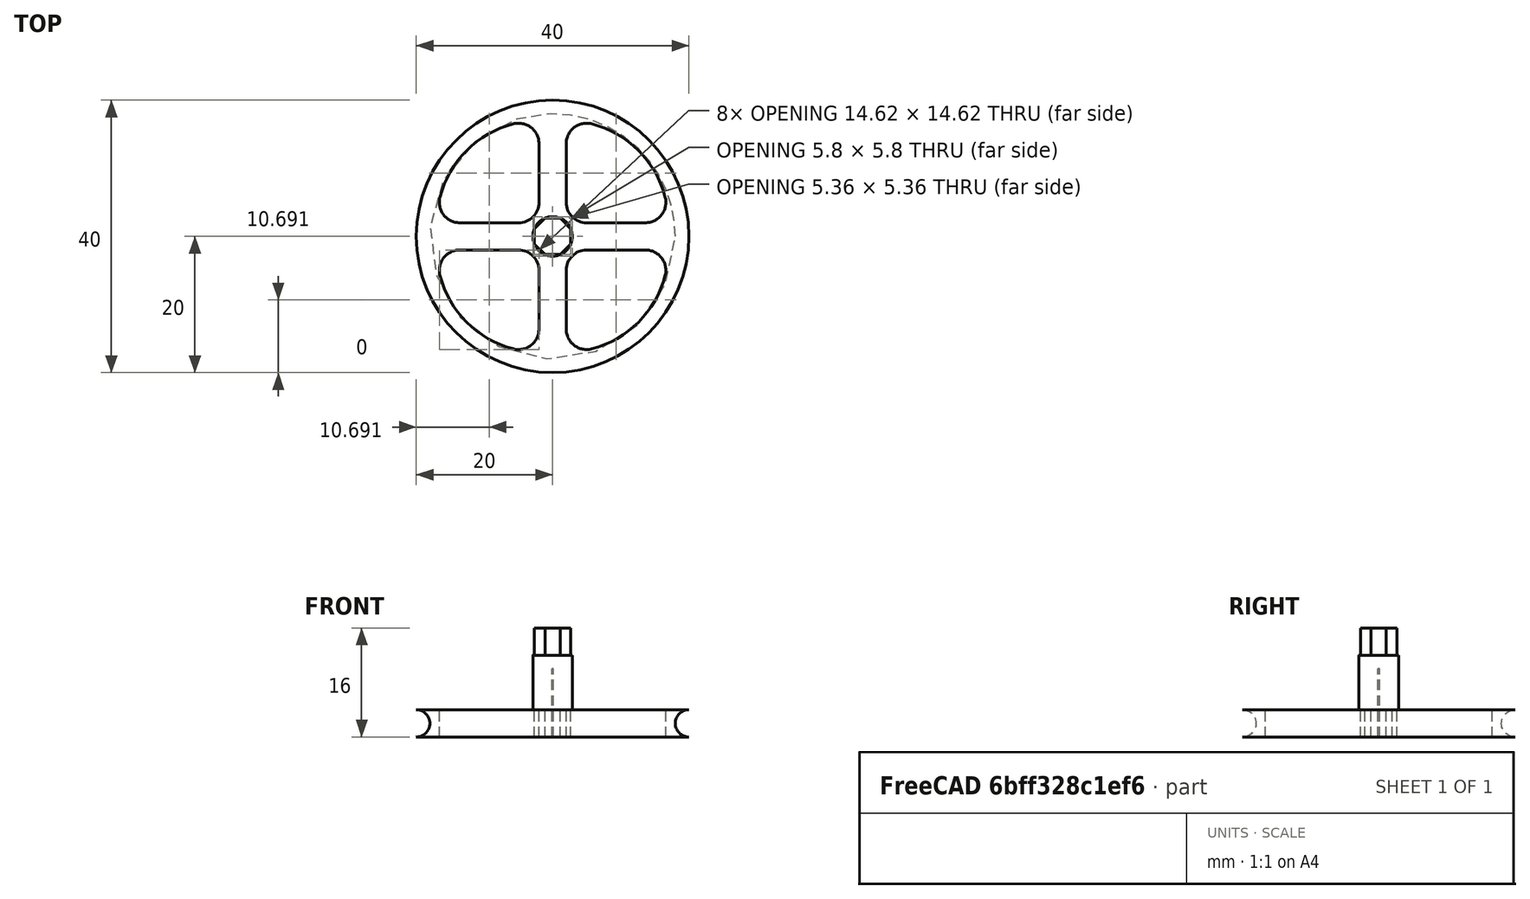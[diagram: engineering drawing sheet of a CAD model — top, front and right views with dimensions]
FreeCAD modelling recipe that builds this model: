
FCSTD DOCUMENT  (FreeCAD 0.18.1R)
Label: wheel right front techdraw
License: All rights reserved
LicenseURL: http://en.wikipedia.org/wiki/All_rights_reserved
objects: TechDraw::DrawViewDimension×7, PartDesign::Plane×4, TechDraw::DrawProjGroupItem×4, Part::Cylinder×3, Sketcher::SketchObject×3, PartDesign::Fillet×3, PartDesign::Body×3, PartDesign::FeatureBase×2, PartDesign::Pocket×2, Part::MultiFuse×2, App::Part×2, Part::Torus×1, Part::Cut×1, App::MeasureDistance×1, PartDesign::ShapeBinder×1, PartDesign::Pad×1, TechDraw::DrawSVGTemplate×1, TechDraw::DrawProjGroup×1, TechDraw::DrawPage×1
note: 29 computed .brp shape members not serialized (recipe doc carries the construction recipe); baked Part::Feature solids carry a one-line shape summary decoded from their .brp

FEATURE [Part::Cylinder] Cylinder
  Angle = 360
  AttacherType = Attacher::AttachEngine3D
  Height = 4
  Radius = 20
FEATURE [Part::Cylinder] Cylinder001
  Angle = 360
  AttacherType = Attacher::AttachEngine3D
  Height = 10
  Radius = 0.1
FEATURE [PartDesign::FeatureBase] BaseFeature
  BaseFeature = -> Cylinder
FEATURE [PartDesign::Plane] DatumPlane
  Length = 47.9863
  MapMode = 5
  Placement = pos=(0,0,0) rot=(1,0,0;3.14159rad)
  ResizeMode = 0
  Support = -> [BaseFeature]
  Width = 47.8497
FEATURE [Sketcher::SketchObject] Sketch001
  MapMode = 5
  Placement = pos=(0,0,0) rot=(1,0,0;3.14159rad)
  Support = -> [DatumPlane]
  sketch-geometry (12):
    g0: LineSegment StartX=2 StartY=17 StartZ=0 EndX=2 EndY=2 EndZ=0
    g1: LineSegment StartX=-2 StartY=17 StartZ=0 EndX=-2 EndY=2 EndZ=0
    g2: LineSegment StartX=2 StartY=2 StartZ=0 EndX=17 EndY=2 EndZ=0
    g3: LineSegment StartX=2 StartY=-2 StartZ=0 EndX=17 EndY=-2 EndZ=0
    g4: LineSegment StartX=-2 StartY=-2 StartZ=0 EndX=-2 EndY=-17 EndZ=0
    g5: LineSegment StartX=-17 StartY=-2 StartZ=0 EndX=-2 EndY=-2 EndZ=0
    g6: LineSegment StartX=-17 StartY=2 StartZ=0 EndX=-2 EndY=2 EndZ=0
    g7: LineSegment StartX=2 StartY=-2 StartZ=0 EndX=2 EndY=-17 EndZ=0
    g8: ArcOfCircle CenterX=2 CenterY=2 CenterZ=0 NormalX=0 NormalY=0 NormalZ=1 AngleXU=0 Radius=15 StartAngle=0 EndAngle=1.5708
    g9: ArcOfCircle CenterX=-2 CenterY=2 CenterZ=0 NormalX=0 NormalY=0 NormalZ=1 AngleXU=0 Radius=15 StartAngle=1.5708 EndAngle=3.14159
    g10: ArcOfCircle CenterX=-2 CenterY=-2 CenterZ=0 NormalX=0 NormalY=0 NormalZ=1 AngleXU=0 Radius=15 StartAngle=3.14159 EndAngle=4.71239
    g11: ArcOfCircle CenterX=2 CenterY=-2 CenterZ=0 NormalX=0 NormalY=0 NormalZ=1 AngleXU=0 Radius=15 StartAngle=4.71239 EndAngle=6.28319
  constraints (35):
    c: Vertical(g0)
    c: Vertical(g1)
    c: Horizontal(g2)
    c: Horizontal(g3)
    c: Vertical(g4)
    c: Horizontal(g6)
    c: DistanceX(g0) = 2
    c: DistanceY(g0) = 17
    c: DistanceY(g0) = 2
    c: Coincident(g0,g2)
    c: DistanceX(g3) = 2
    c: Coincident(g3,g7)
    c: DistanceX(g3) = 17
    c: DistanceY(g7) = -17
    c: DistanceX(g5) = -2
    c: DistanceY(g5) = -2
    c: Coincident(g5,g4)
    c: DistanceY(g4) = -17
    c: DistanceX(g5) = -17
    c: DistanceX(g6) = -2
    c: DistanceX(g6) = -17
    c: DistanceY(g6) = 2
    c: Coincident(g6,g1)
    c: Coincident(g8,g0)
    c: Coincident(g8,g0)
    c: Coincident(g9,g1)
    c: Coincident(g9,g1)
    c: Coincident(g9,g6)
    c: Coincident(g10,g4)
    c: Coincident(g10,g4)
    c: Coincident(g10,g5)
    c: Coincident(g11,g3)
    c: Coincident(g11,g3)
    c: Coincident(g11,g7)
    c: Coincident(g8,g2)
FEATURE [PartDesign::Pocket] Pocket
  BaseFeature = -> BaseFeature
  Length = 5
  Length2 = 100
  Profile = -> Sketch001
  Type = 1
FEATURE [PartDesign::Fillet] Fillet
  Base = -> Pocket [Edge39]
  BaseFeature = -> Pocket
  Radius = 3
FEATURE [PartDesign::Fillet] Fillet001
  Base = -> Fillet [Edge27,Edge39,Edge41,Edge17,Edge26,Edge32,Edge35]
  BaseFeature = -> Fillet
  Radius = 3
FEATURE [PartDesign::Fillet] Fillet002
  Base = -> Fillet001 [Edge56,Edge46,Edge42,Edge30]
  BaseFeature = -> Fillet001
  Radius = 3
FEATURE [PartDesign::Body] Body
  BaseFeature = -> Cylinder
  Group = -> [BaseFeature,DatumPlane,Sketch001,Pocket,Fillet,Fillet001,Fillet002]
  Origin = -> Origin
  Tip = -> Fillet002
FEATURE [Part::Torus] Torus
  Angle1 = -180
  Angle2 = 180
  Angle3 = 360
  AttacherType = Attacher::AttachEngine3D
  Placement = pos=(0,0,2) rot=(0,0,1;0rad)
  Radius1 = 20
  Radius2 = 2
FEATURE [Part::Cut] Cut
  Base = -> Body
  Tool = -> Torus
FEATURE [PartDesign::FeatureBase] BaseFeature001
  BaseFeature = -> Cut
FEATURE [PartDesign::Plane] DatumPlane001
  Length = 24
  MapMode = 5
  Placement = pos=(0,0,0) rot=(1,0,0;3.14159rad)
  ResizeMode = 0
  Support = -> [BaseFeature001]
  Width = 24
FEATURE [PartDesign::Plane] DatumPlane002
  Length = 24
  MapMode = 5
  Placement = pos=(0,0,0) rot=(1,0,0;3.14159rad)
  ResizeMode = 0
  Support = -> [BaseFeature001]
  Width = 24
FEATURE [Sketcher::SketchObject] Sketch
  MapMode = 5
  Placement = pos=(0,0,0) rot=(1,0,0;3.14159rad)
  Support = -> [DatumPlane002]
  sketch-geometry (9):
    g0: LineSegment StartX=1.10978 StartY=-2.67925 StartZ=0 EndX=2.67925 EndY=-1.10978 EndZ=0
    g1: LineSegment StartX=2.67925 StartY=-1.10978 StartZ=0 EndX=2.67925 EndY=1.10978 EndZ=0
    g2: LineSegment StartX=2.67925 StartY=1.10978 StartZ=0 EndX=1.10978 EndY=2.67925 EndZ=0
    g3: LineSegment StartX=1.10978 StartY=2.67925 StartZ=0 EndX=-1.10978 EndY=2.67925 EndZ=0
    g4: LineSegment StartX=-1.10978 StartY=2.67925 StartZ=0 EndX=-2.67925 EndY=1.10978 EndZ=0
    g5: LineSegment StartX=-2.67925 StartY=1.10978 StartZ=0 EndX=-2.67925 EndY=-1.10978 EndZ=0
    g6: LineSegment StartX=-2.67925 StartY=-1.10978 StartZ=0 EndX=-1.10978 EndY=-2.67925 EndZ=0
    g7: LineSegment StartX=-1.10978 StartY=-2.67925 StartZ=0 EndX=1.10978 EndY=-2.67925 EndZ=0
    g8: Circle [constr] CenterX=0 CenterY=0 CenterZ=0 NormalX=0 NormalY=0 NormalZ=1 AngleXU=0 Radius=2.9
  constraints (20):
    c: Coincident(g0,g1)
    c: Coincident(g1,g2)
    c: Coincident(g2,g3)
    c: Coincident(g3,g4)
    c: Coincident(g4,g5)
    c: Coincident(g5,g6)
    c: Coincident(g6,g7)
    c: Coincident(g7,g0)
    c: Equal(g0, g1-g7) x7
    c: PointOnObject(g0,g8)
    c: PointOnObject(g1,g8)
    c: PointOnObject(g2,g8)
    c: PointOnObject(g3,g8)
    c: PointOnObject(g4,g8)
    c: PointOnObject(g5,g8)
    c: PointOnObject(g6,g8)
    c: PointOnObject(g7,g8)
    c: Coincident(g8,g-1)
    c: Radius(g8) = 2.9
    c: DistanceX(g1,g0) = 0
FEATURE [PartDesign::Pocket] Pocket001
  BaseFeature = -> BaseFeature001
  Length = 5
  Length2 = 100
  Profile = -> Sketch
  Type = 0
FEATURE [PartDesign::Body] Body001
  BaseFeature = -> Cut
  Group = -> [BaseFeature001,DatumPlane001,DatumPlane002,Sketch,Pocket001]
  Origin = -> Origin001
  Tip = -> Pocket001
FEATURE [Part::Cylinder] Cylinder002
  Angle = 360
  AttacherType = Attacher::AttachEngine3D
  Height = 12
  Radius = 2.9
FEATURE [App::MeasureDistance] Distance  label="Distance: 4.03 mm"
  Distance = 4.03426
  P1 = (-19.6792,-3.42447,0)
  P2 = (-19.7612,-2.90625,4)
FEATURE [Part::MultiFuse] Fusion
  Shapes = -> [Pocket001,Cylinder002]
FEATURE [App::Part] Part
  Origin = -> Origin002
FEATURE [PartDesign::ShapeBinder] CopyFusion
  TraceSupport = false
FEATURE [PartDesign::Plane] DatumPlane003
  Length = 24
  MapMode = 5
  Placement = pos=(0,0,12) rot=(0,0,1;0rad)
  ResizeMode = 0
  Support = -> [CopyFusion]
  Width = 24
FEATURE [Sketcher::SketchObject] Sketch002
  MapMode = 5
  Placement = pos=(0,0,12) rot=(0,0,1;0rad)
  Support = -> [DatumPlane003]
  sketch-geometry (9):
    g0: LineSegment StartX=1.10978 StartY=2.67925 StartZ=0 EndX=-1.10978 EndY=2.67925 EndZ=0
    g1: LineSegment StartX=-1.10978 StartY=2.67925 StartZ=0 EndX=-2.67925 EndY=1.10978 EndZ=0
    g2: LineSegment StartX=-2.67925 StartY=1.10978 StartZ=0 EndX=-2.67925 EndY=-1.10978 EndZ=0
    g3: LineSegment StartX=-2.67925 StartY=-1.10978 StartZ=0 EndX=-1.10978 EndY=-2.67925 EndZ=0
    g4: LineSegment StartX=-1.10978 StartY=-2.67925 StartZ=0 EndX=1.10978 EndY=-2.67925 EndZ=0
    g5: LineSegment StartX=1.10978 StartY=-2.67925 StartZ=0 EndX=2.67925 EndY=-1.10978 EndZ=0
    g6: LineSegment StartX=2.67925 StartY=-1.10978 StartZ=0 EndX=2.67925 EndY=1.10978 EndZ=0
    g7: LineSegment StartX=2.67925 StartY=1.10978 StartZ=0 EndX=1.10978 EndY=2.67925 EndZ=0
    g8: Circle [constr] CenterX=0 CenterY=0 CenterZ=0 NormalX=0 NormalY=0 NormalZ=1 AngleXU=0 Radius=2.9
  constraints (20):
    c: Coincident(g0,g1)
    c: Coincident(g1,g2)
    c: Coincident(g2,g3)
    c: Coincident(g3,g4)
    c: Coincident(g4,g5)
    c: Coincident(g5,g6)
    c: Coincident(g6,g7)
    c: Coincident(g7,g0)
    c: Equal(g0, g1-g7) x7
    c: PointOnObject(g0,g8)
    c: PointOnObject(g1,g8)
    c: PointOnObject(g2,g8)
    c: PointOnObject(g3,g8)
    c: PointOnObject(g4,g8)
    c: PointOnObject(g5,g8)
    c: PointOnObject(g6,g8)
    c: PointOnObject(g7,g8)
    c: Radius(g8) = 2.9
    c: Coincident(g-1,g8)
    c: DistanceX(g6,g5) = 0
FEATURE [PartDesign::Pad] Pad
  Length = 4
  Length2 = 100
  Placement = pos=(0,0,12) rot=(0,0,1;0rad)
  Profile = -> Sketch002
  Type = 0
FEATURE [PartDesign::Body] Body002
  Group = -> [DatumPlane003,CopyFusion,Sketch002,Pad]
  Origin = -> Origin003
  Tip = -> Pad
FEATURE [App::Part] Part001
  Group = -> [Body002]
  Origin = -> Origin004
FEATURE [Part::MultiFuse] Fusion001
  Shapes = -> [Pad,Fusion]
FEATURE [TechDraw::DrawSVGTemplate] Template
  EditableTexts = Designed_by_Name=Designed by Name; Drawing_number=Drawing number; FC-Date=Date; FC-SC=Scale; FC-SH=Sheet; FC-Title=Title; Subtitle=Subtitle; Weight=Weight
  Height = 210
  Orientation = 1
  Width = 297
FEATURE [TechDraw::DrawProjGroupItem] ProjItem  label="Front"
  CoarseView = false
  Direction = (-1,0,0)
  Focus = 100
  HardHidden = false
  IsoCount = 0
  IsoHidden = false
  IsoVisible = false
  LockPosition = true
  Perspective = false
  Rotation = 0
  RotationVector = (0,-1,0)
  ScaleType = 2
  SeamHidden = false
  SeamVisible = false
  SmoothHidden = false
  SmoothVisible = false
  Source = -> [Fusion001]
  Type = 0
  X = 0
  Y = 0
FEATURE [TechDraw::DrawProjGroupItem] ProjItem001  label="Left"
  CoarseView = false
  Direction = (-1e-16,1,0)
  Focus = 100
  HardHidden = false
  IsoCount = 0
  IsoHidden = false
  IsoVisible = false
  LockPosition = false
  Perspective = false
  Rotation = 0
  RotationVector = (-1,-1e-16,0)
  ScaleType = 2
  SeamHidden = false
  SeamVisible = false
  SmoothHidden = false
  SmoothVisible = false
  Source = -> [Fusion001]
  Type = 1
  X = 55
  Y = 0
FEATURE [TechDraw::DrawProjGroupItem] ProjItem002  label="Top"
  CoarseView = false
  Direction = (0,0,1)
  Focus = 100
  HardHidden = false
  IsoCount = 0
  IsoHidden = false
  IsoVisible = false
  LockPosition = false
  Perspective = false
  Rotation = 0
  RotationVector = (0,-1,0)
  ScaleType = 2
  SeamHidden = false
  SeamVisible = false
  SmoothHidden = false
  SmoothVisible = false
  Source = -> [Fusion001]
  Type = 4
  X = 0
  Y = -55
FEATURE [TechDraw::DrawProjGroupItem] ProjItem003  label="FrontTopLeft"
  CoarseView = false
  Direction = (-1,1,1)
  Focus = 100
  HardHidden = false
  IsoCount = 0
  IsoHidden = false
  IsoVisible = false
  LockPosition = false
  Perspective = false
  Rotation = 0
  RotationVector = (-1,-1,0)
  ScaleType = 2
  SeamHidden = false
  SeamVisible = false
  SmoothHidden = false
  SmoothVisible = false
  Source = -> [Fusion001]
  Type = 6
  X = 55
  Y = -55
FEATURE [TechDraw::DrawProjGroup] ProjGroup
  Anchor = -> ProjItem
  AutoDistribute = true
  LockPosition = false
  ProjectionType = 1
  Rotation = 0
  ScaleType = 0
  Source = -> [Fusion001]
  Views = -> [ProjItem,ProjItem001,ProjItem002,ProjItem003]
  X = 97.784
  Y = 161.884
  spacingX = 15
  spacingY = 15
FEATURE [TechDraw::DrawViewDimension] Dimension
  Arbitrary = false
  FormatSpec = %.2f
  LockPosition = false
  MeasureType = 1
  OverTolerance = 0
  References2D = -> [ProjItem]
  Rotation = 0
  ScaleType = 0
  Type = 2
  UnderTolerance = 0
  X = 9.69016
  Y = 2.66756
FEATURE [TechDraw::DrawViewDimension] Dimension001
  Arbitrary = false
  FormatSpec = %.2f
  LockPosition = false
  MeasureType = 1
  OverTolerance = 0
  References2D = -> [ProjItem]
  Rotation = 0
  ScaleType = 0
  Type = 2
  UnderTolerance = 0
  X = -11.6892
  Y = 8.24318
FEATURE [TechDraw::DrawViewDimension] Dimension002
  Arbitrary = false
  FormatSpec = ⌀%.2f
  LockPosition = false
  MeasureType = 1
  OverTolerance = 0
  References2D = -> [ProjItem002]
  Rotation = 0
  ScaleType = 0
  Type = 5
  UnderTolerance = 0
  X = -0.41905
  Y = -28.6001
FEATURE [TechDraw::DrawViewDimension] Dimension003
  Arbitrary = false
  FormatSpec = R%.2f
  LockPosition = false
  MeasureType = 1
  OverTolerance = 0
  References2D = -> [ProjItem002]
  Rotation = 0
  ScaleType = 0
  Type = 4
  UnderTolerance = 0
  X = -1.15239
  Y = 29.7525
FEATURE [TechDraw::DrawViewDimension] Dimension004
  Arbitrary = false
  FormatSpec = R%.2f
  LockPosition = false
  MeasureType = 1
  OverTolerance = 0
  References2D = -> [ProjItem002]
  Rotation = 0
  ScaleType = 0
  Type = 4
  UnderTolerance = 0
  X = 3.98097
  Y = 25.0382
FEATURE [TechDraw::DrawViewDimension] Dimension005
  Arbitrary = false
  FormatSpec = %.2f
  LockPosition = false
  MeasureType = 1
  OverTolerance = 0
  References2D = -> [ProjItem002]
  Rotation = 0
  ScaleType = 0
  Type = 2
  UnderTolerance = 0
  X = -31.3335
  Y = 13.2904
FEATURE [TechDraw::DrawViewDimension] Dimension006
  Arbitrary = false
  FormatSpec = %.2f
  LockPosition = false
  MeasureType = 1
  OverTolerance = 0
  References2D = -> [ProjItem003]
  Rotation = 0
  ScaleType = 0
  Type = 2
  UnderTolerance = 0
  X = 27.2556
  Y = 8.17829
FEATURE [TechDraw::DrawPage] Page
  KeepUpdated = true
  ProjectionType = 0
  Template = -> Template
  Views = -> [ProjGroup,Dimension,Dimension001,Dimension002,Dimension003,Dimension004,Dimension005,Dimension006]
